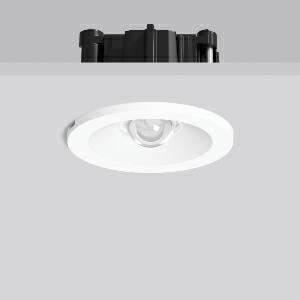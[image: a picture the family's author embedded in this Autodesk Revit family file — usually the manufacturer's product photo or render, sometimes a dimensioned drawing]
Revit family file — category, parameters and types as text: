
# Revit family: turia_l_672411_002_89_bba0
name_source: partatom
category: Lighting Fixtures
units: mm (PartAtom-declared; Revit-internal decimal feet)

## family parameters
Cut with Voids When Loaded = No
Host = Face
Light Source = No
Part Type = Normal
Room Calculation Point = No
Round Connector Dimension = Use Diameter
Shared = No

## types (1)
- TURIA L (1 x LED Modul 765, 250 lm, 6500)
    Apparent Load = 5 VA
    CIE Flux Codes = 17 57 99 100 100
    Color Rendering = 70
    Color Temperature = 6500
    Default Elevation = 1800 mm
    Description = Series: TURIA L
Round emergency luminaire for escape route lighting. With plastic lenses for area lighting. Suitable for connection to central battery systems. With AC Control monitoring module for LUXIFAIR central battery units. With enclosed separate ceiling mounting ring also suitable for ceiling cut-outs of Ø 68 mm. 
Colour: white
Diameter: 62 mm
Height: 3 mm
Cut-out diameter: 54-68 mm
Recess height: 76-162 mm
Luminaire: recess height: 42 mm
Weight: 350 g
Operating mode: non-maintained power mode
Lamp: LED
Socket: without socket
Colour temperature: 6500K
Colour rendering index (CRI): 70
System power: 4.8 W
Rated luminous flux: 250 lm
Luminous flux, emergency: 250 lm
System power, emergency: 4.8 W
Control gear: Regulated power supply
Protection class: II
Type of protection: IP 20
    Height = 0 mm  [stored 0 ft]
    Lamp = 1 x LED Modul 765
    Lamp Light Flux = 250 lm
    Lamp count = 1
    Length = 62 mm  [stored 0.203412 ft]
    Lifetime = 50000 h
    Luminous efficacy = 52 lm/W
    Manufacturer = RZB
    ModVariant = No
    Model = 672411.002.89
    Mounting Place = Ceiling
    Mounting Type = Recessed
    Number of Poles = 1
    OnlyDefault = Yes
    Power Factor = 1
    Product Name = TURIA L
    Product group = Recessed ceiling luminaires
    ProductGroupID = 405
    Protection Class = Protection class II
    Protection Degree = IP 20
    RLX_Detail_Level = 1
    RLX_Emergency_Light_Flux = 250 lm
    RLX_Emergency_Type = 3
    RLX_Emergency_Type_DB = Yes
    RlxData = <blob elided: 35305 chars, md5=7afbeeb5>
    Socket = socket
    Standby Power = 0 W
    System Light Flux = 250 lm
    System Power = 5 W
    Type Comments = Product without accessories
    Type Image = 672412.002.jpg
    URL = http://relux.com
    VarID = ---
    Voltage = 230 V
    Voltage Range = 220-240 V
    Weight = 0.00 kg
    Width = 0 mm  [stored 0 ft]

note: [stored X ft] marks values corroborated as IEEE doubles in the binary element streams (Revit-internal decimal feet)

## geometry (parser evidence)
native form markers: Blend x4, Sweep x9
no freeform markers — native parametric forms only
